# Revit family: PRD_AR_PprTwlDspnsrs_STRATOSPaperTowelDispenser_STR637_STR635B
name_source: partatom
category: Specialty Equipment
units: mm (PartAtom-declared; Revit-internal decimal feet)

## family parameters
Cut with Voids When Loaded = No
Host = Face
OmniClass Number = 23.40.20.21.17
OmniClass Title = Paper Towel Dispensers, Disposal Units
Part Type = Normal
Room Calculation Point = No
Round Connector Dimension = Use Diameter
Shared = No

## types (2) — shared parameters
AssetType = Fixed
Category = Pr_40_70_22_62, Paper Towel Dispensers
Default Elevation = 900 mm  [stored 2.95276 ft]
DispenserMaterial = PRD_AR_StainlessSteel_SatinFinished
DurationUnit = year
Features = stainless steel, surface satin finished
FillingQuantity = 1
FillingQuantityUom = Rolls
Finish = satin finished
IfcExportAs = IfcFurnitureType
IfcExportType = USERDEFINED
IntegralAccessories = incl. stainless steel screws and dowels
IsBuiltIn = TRUE
Lock = Key-lock
MainColor = stainless steel
Manufacturer = KWC Group Management AG
ManufacturerName = KWC Group Management AG
ManufacturerURL = www.kwc-professional.com
Material = stainless steel
MaterialCode = 1.4301
MaterialThickness = 1.50 mm
NBSDescription = Paper towel dispensers
NBSReference = 45-35-72/344
ProductInformation = http://pim.kwc.com
Style = dispenser
TypeOfConsumable = Paper roll
TypeOfFixing = Screw
TypeOfMounting = Wall mounting
TypeOfOperation = Manual operation
URL = www.kwc-professional.com
Uniclass2015Code = Pr_40_70_22_62
Uniclass2015Title = Paper towel dispensers
Uniclass2015Version = Products v1.10
Version = 1
WarrantyDurationUnit = year

## per-type parameters (varying)
| type | BIMObjectName | Description | GrossWeight | MaximumDepthDiameterOfConsumable | MaximumWidthOfConsumable | ModelNumber | Name | NetWeight | NominalDepth | NominalHeight | NominalWidth | Size |
| STR637 | PRD_AR_PaperTowelDispensers_STRATOSPaperTowelDispenser_STR637 | STRATOS paper towel dispenser for wall mounting, stainless steel, surface satin finished, material thickness 1.5 mm, curved front with inspection window, cylinder lock with key, capacity one paper roll, paper is transported automatically - to be pulled by hand, maintenance-free mechanism, no electrical connections or batteries required, easy roll change mechanism for rolls with maximum width 205 mm and maximum diameter 200 mm, fixed paper tear-off length 260 mm, adjustable paper roll holder for optimised paper dispensing, including mounting material. | 7.77 kg | 200.00 mm | 205.00 mm | 3600008866 | STRATOS Paper Towel Dispenser STR637 | 7.16 kg | 227 mm  [stored 0.744751 ft] | 385 mm  [stored 1.26312 ft] | 294 mm  [stored 0.964567 ft] | 294 x 385 x 227 mm |
| STR635B | PRD_AR_PaperTowelDispensers_STRATOSPaperTowelDispenser_STR635B | STRATOS paper roll box for wall mounting, stainless steel, surface satin finished, material thickness 1.5 mm, curved front, cylinder lock with key, for paper rolls with maximum diameter 190 and maximum height 250 mm, only suitable for paper rolls with unwinding from the centre, integrated tear-off edge and strain relief to prevent paper tearing in the housing, including mounting material. | 5.32 kg | 190.00 mm | 250.00 mm | 3600008865 | STRATOS Paper Towel Dispenser STR635B | 4.70 kg | 240 mm  [stored 0.787402 ft] | 343 mm  [stored 1.12533 ft] | 205 mm  [stored 0.672572 ft] | 205 x 343 x 240 mm |

note: column(s) folded — value = type name in every type: Model, ModelReference, Type

note: [stored X ft] marks values corroborated as IEEE doubles in the binary element streams (Revit-internal decimal feet)

## geometry (parser evidence)
native form markers: Sweep x9
no freeform markers — native parametric forms only
